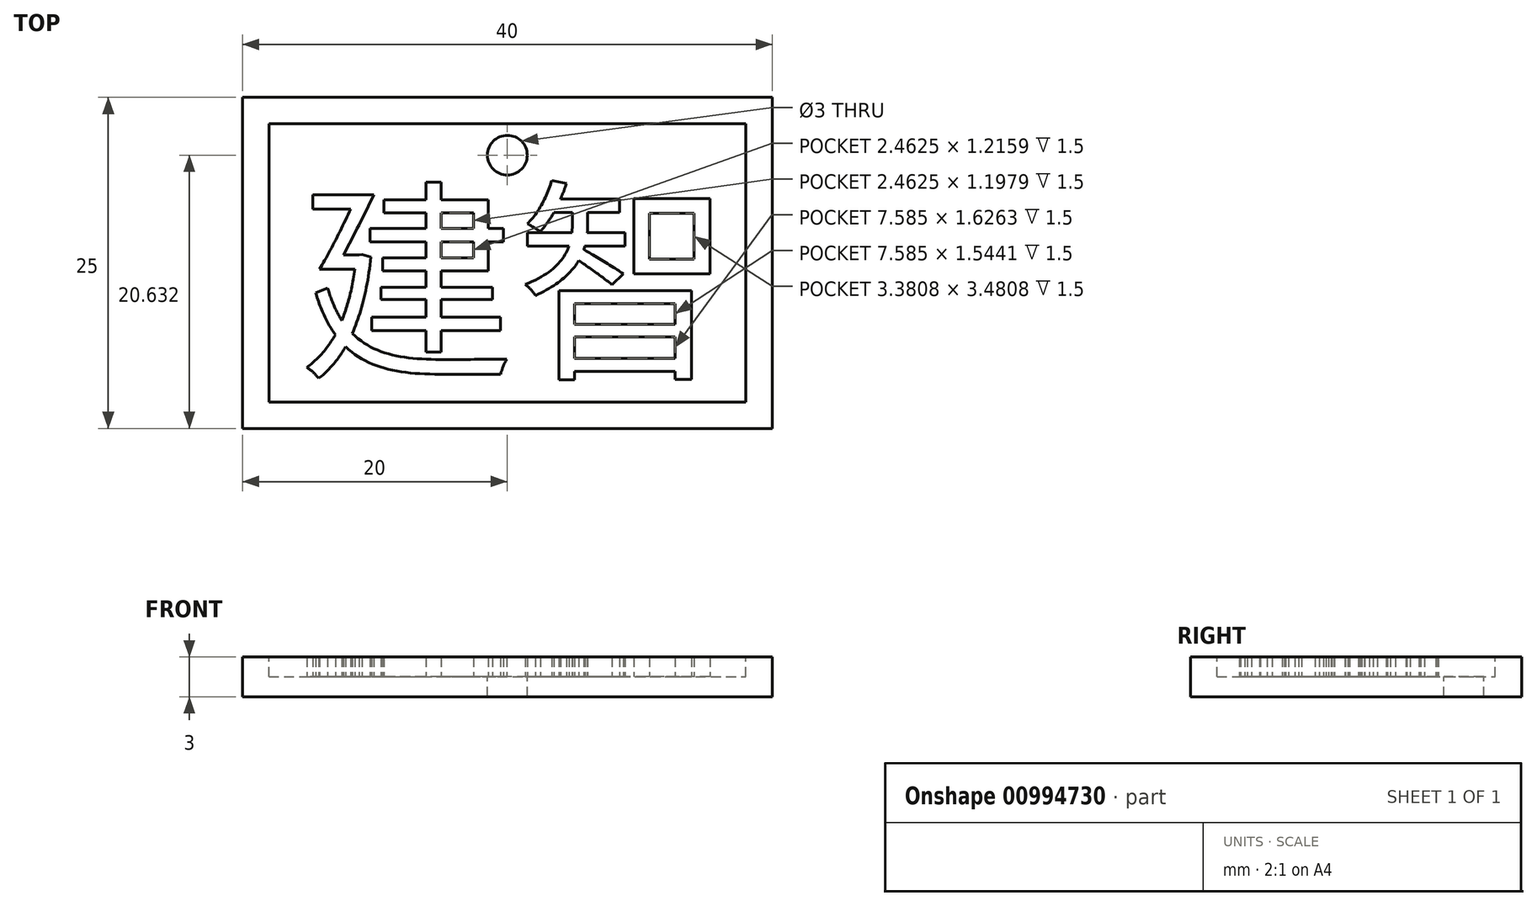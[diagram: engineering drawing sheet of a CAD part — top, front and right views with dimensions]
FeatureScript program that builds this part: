
annotation { "Feature Type Name" : "Feature", "Feature Type Description" : "" }
export const myFeature = defineFeature(function(context is Context, id is Id, definition is map)
    precondition{}
    {
        {
            var Q0;
            Q0=qCreatedBy(makeId("Top.planeOp"),FACE);
            var sketch = newSketch(context, id + "F0", { "sketchPlane" : qUnion([Q0])});
            skLineSegment(sketch, "E0.bottom", {"start": v(20, -12.5) * mm, "end": v(-20, -12.5) * mm});
            skLineSegment(sketch, "E0.top", {"start": v(20, 12.5) * mm, "end": v(-20, 12.5) * mm});
            skLineSegment(sketch, "E0.left", {"start": v(20, -12.5) * mm, "end": v(20, 12.5) * mm});
            skLineSegment(sketch, "E0.right", {"start": v(-20, -12.5) * mm, "end": v(-20, 12.5) * mm});
            skPoint(sketch, "E0.middle", {"position": v(0, 0) * mm});
            skSolve(sketch);
        }
        {
            var Q0;
            Q0 = qSketchRegion(id + "F0", true);
            extrude(context, id + "F1", {"entities" : qUnion([Q0]), "depth" : 3 * mm, "offsetDistance" : 25 * mm});
        }
        {
            var Q0;
            Q0=makeQuery(id+"F1.opExtrude","CAP_FACE",FACE,{"disambiguationData":[OSD([sQuery(id+"F0.wireOp",EDGE,"E0.bottom"),sQuery(id+"F0.wireOp",EDGE,"E0.top"),sQuery(id+"F0.wireOp",EDGE,"E0.left"),sQuery(id+"F0.wireOp",EDGE,"E0.right")])],"isStart":false});
            var sketch = newSketch(context, id + "F2", { "sketchPlane" : qUnion([Q0])});
            skLineSegment(sketch, "E1.0", {"start": v(18, -10.5) * mm, "end": v(18, 10.5) * mm});
            skLineSegment(sketch, "E1.1", {"start": v(-18, -10.5) * mm, "end": v(18, -10.5) * mm});
            skLineSegment(sketch, "E1.2", {"start": v(-18, 10.5) * mm, "end": v(-18, -10.5) * mm});
            skLineSegment(sketch, "E1.3", {"start": v(18, 10.5) * mm, "end": v(-18, 10.5) * mm});
            skSolve(sketch);
        }
        {
            var Q0;
            Q0 = qSketchRegion(id + "F2", true);
            extrude(context, id + "F3", {"entities" : qUnion([Q0]), "operationType" : NewBodyOperationType.REMOVE, "oppositeDirection" : true, "depth" : 1.5 * mm, "offsetDistance" : 25 * mm});
        }
        {
            var Q0;
            Q0=makeQuery(id+"F3.boolean.opBoolean","COPY",FACE,{"derivedFrom":makeQuery(id+"F3.opExtrude","CAP_FACE",FACE,{"disambiguationData":[OSD([sQuery(id+"F2.wireOp",EDGE,"E1.0"),sQuery(id+"F2.wireOp",EDGE,"E1.1"),sQuery(id+"F2.wireOp",EDGE,"E1.2"),sQuery(id+"F2.wireOp",EDGE,"E1.3")])],"isStart":false})});
            var sketch = newSketch(context, id + "F4", { "sketchPlane" : qUnion([Q0])});
            skCircle(sketch, "E2", {"center": v(0, 8.13) * mm, "radius": 1.5 * mm});
            skSolve(sketch);
        }
        {
            var Q0;
            Q0 = qSketchRegion(id + "F4", true);
            extrude(context, id + "F5", {"entities" : qUnion([Q0]), "operationType" : NewBodyOperationType.REMOVE, "endBound" : BoundingType.THROUGH_ALL, "oppositeDirection" : true, "depth" : 25 * mm, "offsetDistance" : 25 * mm});
        }
        {
            var Q0;
            Q0=makeQuery(id+"F3.boolean.opBoolean","COPY",FACE,{"derivedFrom":makeQuery(id+"F3.opExtrude","CAP_FACE",FACE,{"disambiguationData":[OSD([sQuery(id+"F2.wireOp",EDGE,"E1.0"),sQuery(id+"F2.wireOp",EDGE,"E1.1"),sQuery(id+"F2.wireOp",EDGE,"E1.2"),sQuery(id+"F2.wireOp",EDGE,"E1.3")])],"isStart":false})});
            var sketch = newSketch(context, id + "F6", { "sketchPlane" : qUnion([Q0])});
            skText(sketch, "E3", { "text": "建智", "fontName": "NotoSansCJKtc-Regular.otf"});
            const initialGuessF6  = {"E3": [-0.01579, -0.00755, 1, 0, 0.01182]};
            skSetInitialGuess(sketch, initialGuessF6);
            skSolve(sketch);
        }
        {
            var Q0;
            Q0 = qSketchRegion(id + "F6", true);
            extrude(context, id + "F7", {"entities" : qUnion([Q0]), "operationType" : NewBodyOperationType.ADD, "depth" : 1.5 * mm, "offsetDistance" : 25 * mm});
        }
    });
